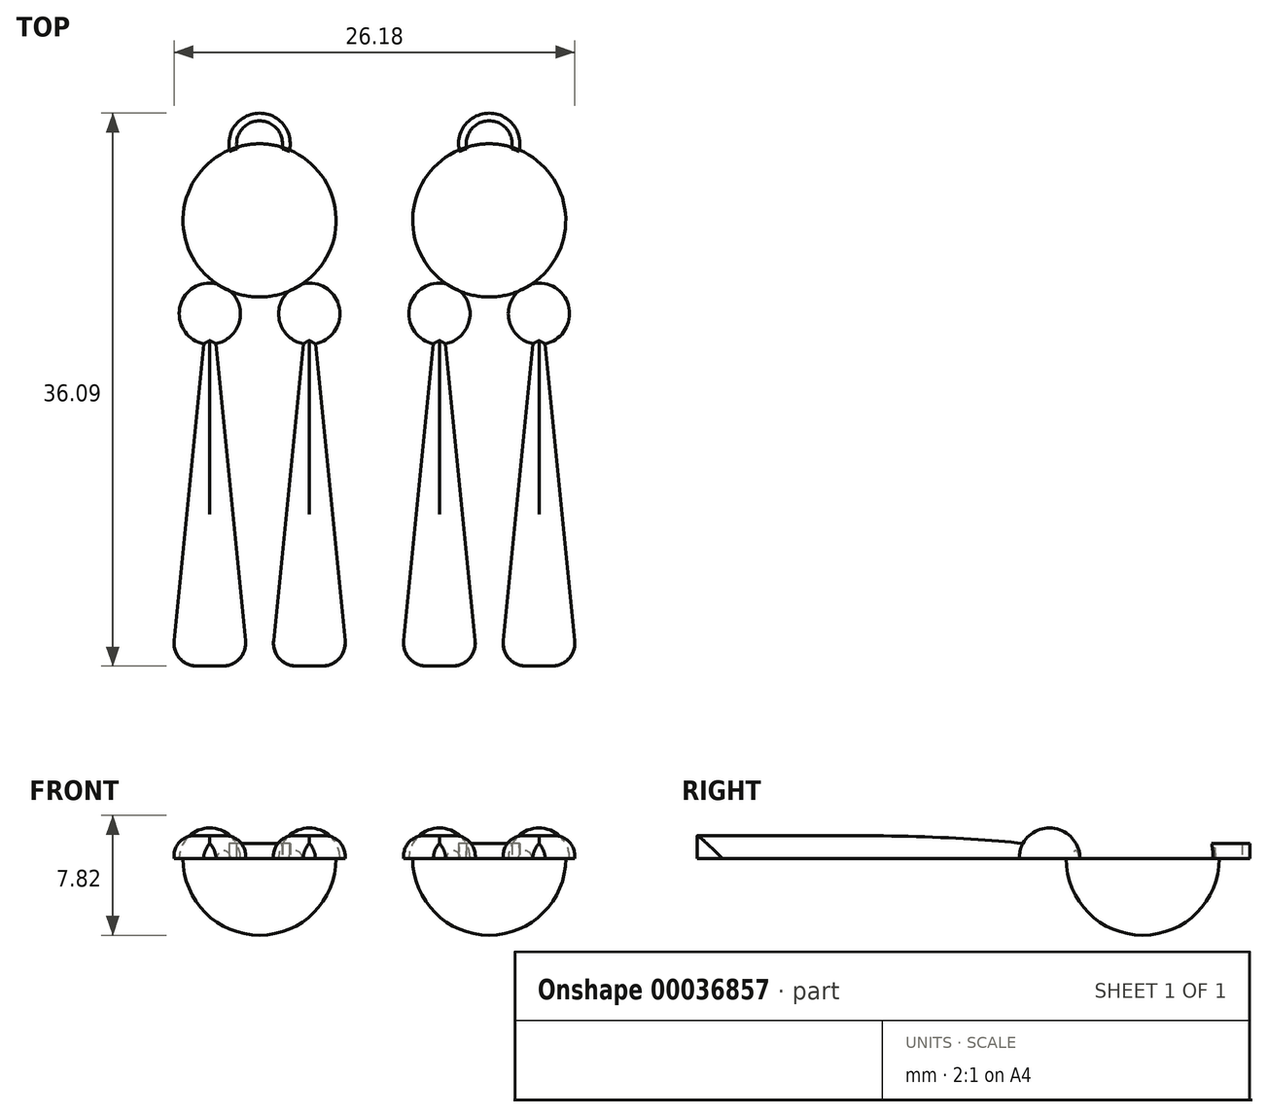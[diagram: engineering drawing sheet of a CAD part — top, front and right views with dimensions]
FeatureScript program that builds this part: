
annotation { "Feature Type Name" : "Feature", "Feature Type Description" : "" }
export const myFeature = defineFeature(function(context is Context, id is Id, definition is map)
    precondition{}
    {
        {
            var Q0;
            Q0=qCreatedBy(makeId("Top.planeOp"),FACE);
            var sketch = newSketch(context, id + "F0", { "sketchPlane" : qUnion([Q0])});
            skLineSegment(sketch, "E0", {"start": v(0, 5.1) * mm, "end": v(0, -4.9) * mm});
            skArc(sketch, "E1", {"start": v(0, 5.1) * mm, "mid": v(-5, 0.1) * mm, "end": v(0, -4.9) * mm});
            skSolve(sketch);
        }
        {
            var Q0;
            Q0 = qSketchRegion(id + "F0", true);
            var Q1;
            Q1=sQuery(id+"F0.wireOp",EDGE,"E0");
            revolve(context, id + "F1", {"entities" : qUnion([Q0]), "axis" : qUnion([Q1]), "revolveType" : RevolveType.ONE_DIRECTION, "oppositeDirection" : true, "angle" : 180 * degree});
        }
        {
            var Q0;
            Q0=qCreatedBy(makeId("Top.planeOp"),FACE);
            var sketch = newSketch(context, id + "F2", { "sketchPlane" : qUnion([Q0])});
            skCircle(sketch, "E2.0", {"center": v(0, 0.1) * mm, "radius": 5 * mm, "construction": true});
            skCircle(sketch, "E3", {"center": v(0, 5.1) * mm, "radius": 1.5 * mm});
            skCircle(sketch, "E4", {"center": v(0, 5.1) * mm, "radius": 2 * mm});
            skSolve(sketch);
        }
        {
            var Q0;
            Q0 = qSketchRegion(id + "F2", true);
            extrude(context, id + "F3", {"entities" : qUnion([Q0]), "operationType" : NewBodyOperationType.ADD, "depth" : 1 * mm});
        }
        {
            var Q0;
            Q0=qCreatedBy(makeId("Top.planeOp"),FACE);
            var sketch = newSketch(context, id + "F4", { "sketchPlane" : qUnion([Q0])});
            skLineSegment(sketch, "E5", {"start": v(0, 0) * mm, "end": v(0, -6) * mm, "construction": true});
            skLineSegment(sketch, "E6", {"start": v(-3.25, -6) * mm, "end": v(3.25, -6) * mm, "construction": true});
            skLineSegment(sketch, "E7", {"start": v(-3.25, -4) * mm, "end": v(-3.25, -8) * mm});
            skArc(sketch, "E8", {"start": v(-3.25, -4) * mm, "mid": v(-5.25, -6) * mm, "end": v(-3.25, -8) * mm});
            skLineSegment(sketch, "E9.MirrorCS", {"start": v(3.25, -4) * mm, "end": v(3.25, -8) * mm});
            skArc(sketch, "E10.MirrorCS", {"start": v(3.25, -4) * mm, "mid": v(5.25, -6) * mm, "end": v(3.25, -8) * mm});
            skSolve(sketch);
        }
        {
            var Q0;
            Q0=qCreatedBy(makeId("Top.planeOp"),FACE);
            var sketch = newSketch(context, id + "F5", { "sketchPlane" : qUnion([Q0])});
            skLineSegment(sketch, "E11.0", {"start": v(0, 0) * mm, "end": v(0, -6) * mm, "construction": true});
            skLineSegment(sketch, "E12", {"start": v(-3.25, -4) * mm, "end": v(-3.25, -29) * mm, "construction": true});
            skLineSegment(sketch, "E13", {"start": v(-5.75, -29) * mm, "end": v(-0.75, -29) * mm});
            skLineSegment(sketch, "E14", {"start": v(-3.25, -4) * mm, "end": v(-5.75, -29) * mm});
            skLineSegment(sketch, "E15", {"start": v(-0.75, -29) * mm, "end": v(-3.25, -4) * mm});
            skLineSegment(sketch, "E16.MirrorCS", {"start": v(0.75, -29) * mm, "end": v(3.25, -4) * mm});
            skLineSegment(sketch, "E17.MirrorCS", {"start": v(3.25, -4) * mm, "end": v(5.75, -29) * mm});
            skLineSegment(sketch, "E18.MirrorCS", {"start": v(5.75, -29) * mm, "end": v(0.75, -29) * mm});
            skPoint(sketch, "E19.0", {"position": v(-3.25, -4) * mm});
            skPoint(sketch, "E20.0", {"position": v(3.25, -4) * mm});
            skSolve(sketch);
        }
        {
            var Q0;
            Q0 = qSketchRegion(id + "F5", true);
            extrude(context, id + "F6", {"entities" : qUnion([Q0]), "operationType" : NewBodyOperationType.ADD, "depth" : 1.5 * mm});
        }
        {
            var Q0;
            Q0=makeQuery(id+"F6.opExtrude","SWEPT_EDGE",EDGE,{"disambiguationData":[OSD([sQuery(id+"F5.wireOp",EDGE,"E13"),sQuery(id+"F5.wireOp",EDGE,"E14")])]});
            var Q1;
            Q1=makeQuery(id+"F6.opExtrude","SWEPT_EDGE",EDGE,{"disambiguationData":[OSD([sQuery(id+"F5.wireOp",EDGE,"E13"),sQuery(id+"F5.wireOp",EDGE,"E15")])]});
            var Q2;
            Q2=makeQuery(id+"F6.opExtrude","SWEPT_EDGE",EDGE,{"disambiguationData":[OSD([sQuery(id+"F5.wireOp",EDGE,"E16.MirrorCS"),sQuery(id+"F5.wireOp",EDGE,"E18.MirrorCS")])]});
            var Q3;
            Q3=makeQuery(id+"F6.opExtrude","SWEPT_EDGE",EDGE,{"disambiguationData":[OSD([sQuery(id+"F5.wireOp",EDGE,"E17.MirrorCS"),sQuery(id+"F5.wireOp",EDGE,"E18.MirrorCS")])]});
            var Q4;
            Q4=makeQuery(id+"F6.opExtrude","CAP_EDGE",EDGE,{"disambiguationData":[OSD([sQuery(id+"F5.wireOp",EDGE,"E14")])],"isStart":false});
            var Q5;
            Q5=makeQuery(id+"F6.opExtrude","CAP_EDGE",EDGE,{"disambiguationData":[OSD([sQuery(id+"F5.wireOp",EDGE,"E15")])],"isStart":false});
            var Q6;
            Q6=makeQuery(id+"F6.opExtrude","CAP_EDGE",EDGE,{"disambiguationData":[OSD([sQuery(id+"F5.wireOp",EDGE,"E16.MirrorCS")])],"isStart":false});
            var Q7;
            Q7=makeQuery(id+"F6.opExtrude","CAP_EDGE",EDGE,{"disambiguationData":[OSD([sQuery(id+"F5.wireOp",EDGE,"E17.MirrorCS")])],"isStart":false});
            fillet(context, id + "F7", {"entities" : qUnion([Q0, Q1, Q2, Q3, Q4, Q5, Q6, Q7]), "radius" : 1.5 * mm, "tangentPropagation" : true, "allowEdgeOverflow" : false});
        }
        {
            var Q0;
            Q0=makeQuery(id+"F4.imprint","IMPRINT",FACE,{"disambiguationData":[TD([[makeQuery(id+"F4.imprint","IMPRINT",EDGE,{"derivedFrom":sQuery(id+"F4.wireOp",EDGE,"E9.MirrorCS")}),1.0]])]});
            var Q1;
            Q1=sQuery(id+"F4.wireOp",EDGE,"E9.MirrorCS");
            revolve(context, id + "F8", {"operationType" : NewBodyOperationType.ADD, "entities" : qUnion([Q0]), "axis" : qUnion([Q1]), "revolveType" : RevolveType.ONE_DIRECTION, "angle" : 180 * degree});
        }
        {
            var Q0;
            Q0=makeQuery(id+"F4.imprint","IMPRINT",FACE,{"disambiguationData":[TD([[makeQuery(id+"F4.imprint","IMPRINT",EDGE,{"derivedFrom":sQuery(id+"F4.wireOp",EDGE,"E7")}),-1.0]])]});
            var Q1;
            Q1=sQuery(id+"F4.wireOp",EDGE,"E7");
            revolve(context, id + "F9", {"operationType" : NewBodyOperationType.ADD, "entities" : qUnion([Q0]), "axis" : qUnion([Q1]), "revolveType" : RevolveType.ONE_DIRECTION, "oppositeDirection" : true, "angle" : 180 * degree});
        }
        {
            var Q0;
            Q0=makeQuery(id+"F1.opRevolve","SWEPT_BODY",BODY,{"disambiguationData":[OSD([sQuery(id+"F0.wireOp",EDGE,"E0"),sQuery(id+"F0.wireOp",EDGE,"E1")])]});
            transform(context, id + "F10", {"entities" : qUnion([Q0]), "transformType" : TransformType.TRANSLATION_3D, "dx" : 15 * mm, "dy" : 0 * mm, "dz" : 0 * mm, "makeCopy" : true});
        }
    });
